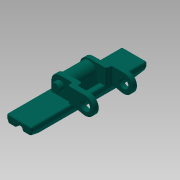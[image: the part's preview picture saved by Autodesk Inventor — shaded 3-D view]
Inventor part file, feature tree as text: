
AUTODESK INVENTOR PART (.ipt)
format: ipt  version: 2013 (Build 170138000, 138)  size: 1,100,800 bytes
history: native  units: mm (DEFAULTED — no unit token found)
features: other x8, plane x3, sketch x2, projected_geometry x2, extrude x2, imported_body x1
ambient origin geometry x8: Origin, YZ Plane, XZ Plane, XY Plane, X Axis, Y Axis, Z Axis, Center Point
bodies: Solid1 (feature_tree)
feature tree (18):
  imported_body  "Base1"
  plane  "Work Plane1"
  plane  "Work Plane2"
  other  "Work Axis2"
  sketch  "Sketch2"  dims[d2=90.0deg d4=5.0mm]
  other  "Work Axis3"
  other  "Work Axis4"
  plane  "Work Plane3"
  sketch  "Sketch3"  dims[d5=2.54mm d6=2.54mm d7=2.54mm d8=0.0mm d9=2.54mm d10=0.0mm d11=0.0mm d12=0.0mm]
  other  "Constrain at start point"
  other  "Constrain on path"
  other  "Work Axis1"
  projected_geometry  "Projected Loop2"
  projected_geometry  "Projected Loop3"
  other  "Srf1"
  other  "Srf2"
  extrude  "ExtrusionSrf1"  Depth=5.0mm
  extrude  "ExtrusionSrf2"  Depth=2.54mm
